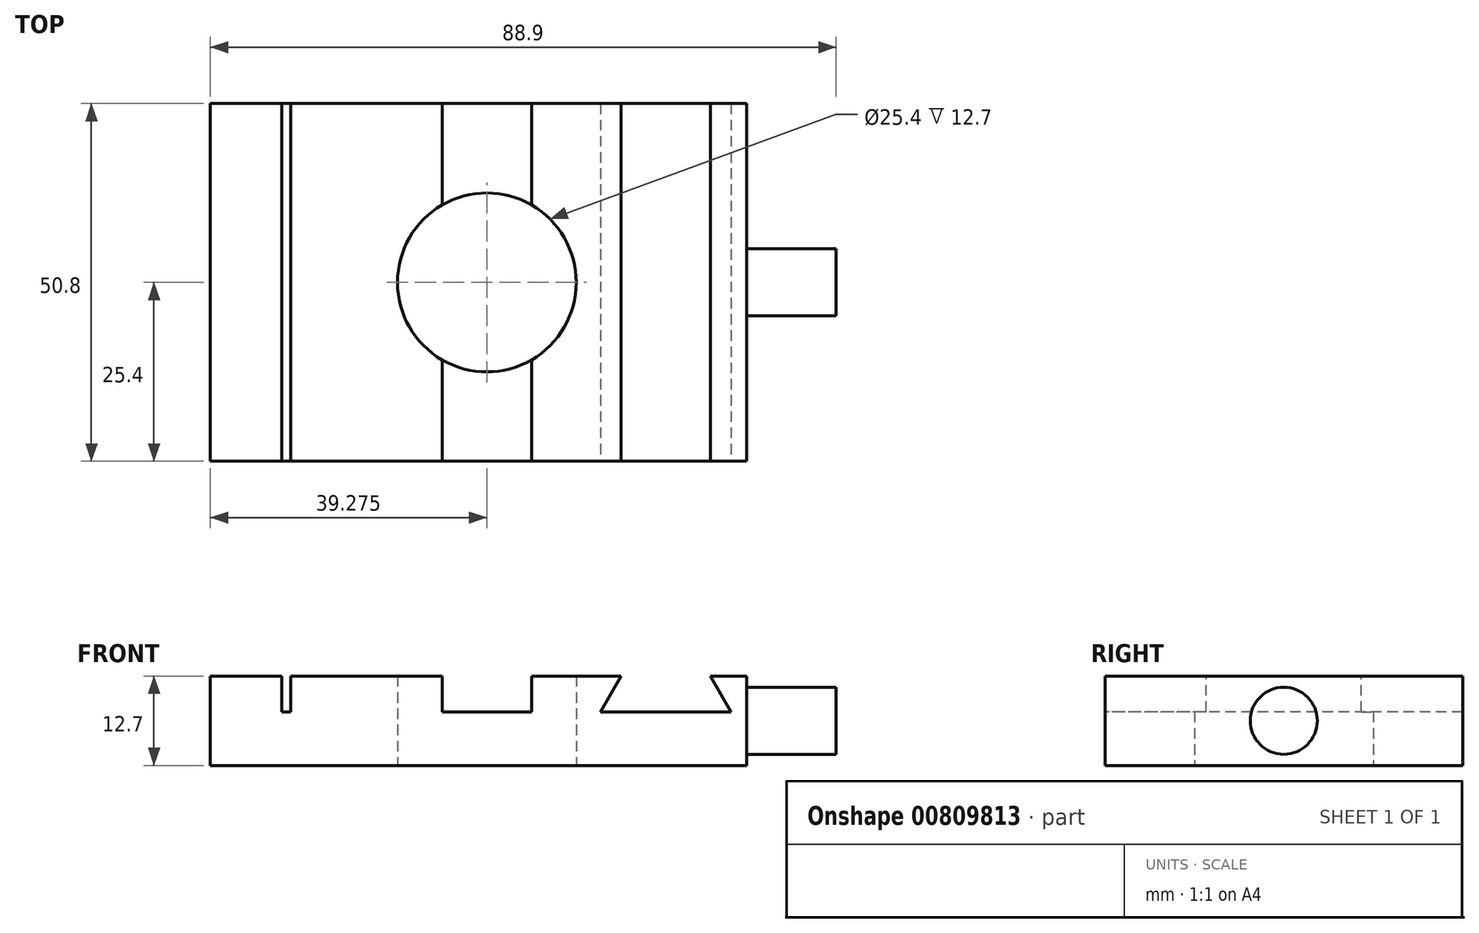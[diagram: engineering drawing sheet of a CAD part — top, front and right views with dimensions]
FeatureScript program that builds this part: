
annotation { "Feature Type Name" : "Feature", "Feature Type Description" : "" }
export const myFeature = defineFeature(function(context is Context, id is Id, definition is map)
    precondition{}
    {
        {
            var Q0;
            Q0=qCreatedBy(makeId("Top.planeOp"),FACE);
            var sketch = newSketch(context, id + "F0", { "sketchPlane" : qUnion([Q0])});
            skLineSegment(sketch, "E0.bottom", {"start": v(-38.1, -25.4) * mm, "end": v(38.1, -25.4) * mm});
            skLineSegment(sketch, "E0.top", {"start": v(-38.1, 25.4) * mm, "end": v(38.1, 25.4) * mm});
            skLineSegment(sketch, "E0.left", {"start": v(-38.1, -25.4) * mm, "end": v(-38.1, 25.4) * mm});
            skLineSegment(sketch, "E0.right", {"start": v(38.1, -25.4) * mm, "end": v(38.1, 25.4) * mm});
            skPoint(sketch, "E0.middle", {"position": v(0, 0) * mm});
            skCircle(sketch, "E1", {"center": v(1.17, 0) * mm, "radius": 12.7 * mm});
            skSolve(sketch);
        }
        {
            var Q0;
            Q0=makeQuery(id+"F0.imprint","IMPRINT",FACE,{"disambiguationData":[TD([[makeQuery(id+"F0.imprint","IMPRINT",EDGE,{"derivedFrom":sQuery(id+"F0.wireOp",EDGE,"E0.bottom")}),1.0]])]});
            extrude(context, id + "F1", {"entities" : qUnion([Q0]), "depth" : 12.7 * mm, "offsetDistance" : 25.4 * mm});
        }
        {
            var Q0;
            Q0=makeQuery(id+"F1.opExtrude","CAP_FACE",FACE,{"disambiguationData":[OSD([sQuery(id+"F0.wireOp",EDGE,"E0.bottom"),sQuery(id+"F0.wireOp",EDGE,"E0.top"),sQuery(id+"F0.wireOp",EDGE,"E0.left"),sQuery(id+"F0.wireOp",EDGE,"E0.right"),sQuery(id+"F0.wireOp",EDGE,"E1")])],"isStart":false});
            var sketch = newSketch(context, id + "F2", { "sketchPlane" : qUnion([Q0])});
            skLineSegment(sketch, "E2.bottom", {"start": v(-27.94, 25.4) * mm, "end": v(-26.67, 25.4) * mm});
            skLineSegment(sketch, "E2.top", {"start": v(-27.94, -25.4) * mm, "end": v(-26.67, -25.4) * mm});
            skLineSegment(sketch, "E2.left", {"start": v(-27.94, 25.4) * mm, "end": v(-27.94, -25.4) * mm});
            skLineSegment(sketch, "E2.right", {"start": v(-26.67, 25.4) * mm, "end": v(-26.67, -25.4) * mm});
            skLineSegment(sketch, "E3", {"start": v(-5.18, 25.4) * mm, "end": v(-5.18, -25.4) * mm});
            skLineSegment(sketch, "E4", {"start": v(-5.18, -25.4) * mm, "end": v(7.52, -25.4) * mm});
            skLineSegment(sketch, "E5", {"start": v(7.52, -25.4) * mm, "end": v(7.52, 25.4) * mm});
            skLineSegment(sketch, "E6", {"start": v(7.52, 25.4) * mm, "end": v(-5.18, 25.4) * mm});
            skLineSegment(sketch, "E7", {"start": v(1.17, 25.4) * mm, "end": v(1.17, -25.4) * mm, "construction": true});
            skPoint(sketch, "E8", {"position": v(1.17, 0) * mm});
            skSolve(sketch);
        }
        {
            var Q0;
            Q0=makeQuery(id+"F2.imprint","IMPRINT",FACE,{"disambiguationData":[TD([[makeQuery(id+"F2.imprint","IMPRINT",EDGE,{"derivedFrom":sQuery(id+"F2.wireOp",EDGE,"E2.bottom")}),-1.0]])]});
            var Q1;
            {var subQ0=sQuery(id+"F2.wireOp",EDGE,"E4");Q1=makeQuery(id+"F2.imprint","IMPRINT",FACE,{"disambiguationData":[TD([[makeQuery(id+"F2.imprint","IMPRINT",EDGE,{"derivedFrom":subQ0}),1.0]])]});}
            var Q2;
            {var subQ0=sQuery(id+"F2.wireOp",EDGE,"E6");Q2=makeQuery(id+"F2.imprint","IMPRINT",FACE,{"disambiguationData":[TD([[makeQuery(id+"F2.imprint","IMPRINT",EDGE,{"derivedFrom":subQ0}),-1.0]])]});}
            extrude(context, id + "F3", {"entities" : qUnion([Q0, Q1, Q2]), "operationType" : NewBodyOperationType.REMOVE, "oppositeDirection" : true, "depth" : 5.08 * mm, "offsetDistance" : 25.4 * mm});
        }
        {
            var Q0;
            Q0=makeQuery(id+"F1.opExtrude","SWEPT_FACE",FACE,{"disambiguationData":[OSD([sQuery(id+"F0.wireOp",EDGE,"E0.bottom")])]});
            var sketch = newSketch(context, id + "F4", { "sketchPlane" : qUnion([Q0])});
            skLineSegment(sketch, "E9", {"start": v(20.22, 12.7) * mm, "end": v(17.3, 7.62) * mm});
            skLineSegment(sketch, "E10", {"start": v(17.3, 7.62) * mm, "end": v(35.86, 7.62) * mm});
            skLineSegment(sketch, "E11", {"start": v(35.86, 7.62) * mm, "end": v(32.92, 12.7) * mm});
            skLineSegment(sketch, "E12", {"start": v(32.92, 12.7) * mm, "end": v(20.22, 12.7) * mm});
            skLineSegment(sketch, "E13", {"start": v(26.57, 7.62) * mm, "end": v(26.57, 12.7) * mm, "construction": true});
            skSolve(sketch);
        }
        {
            var Q0;
            Q0=makeQuery(id+"F4.imprint","IMPRINT",FACE,{"disambiguationData":[TD([[makeQuery(id+"F4.imprint","IMPRINT",EDGE,{"derivedFrom":sQuery(id+"F4.wireOp",EDGE,"E9")}),1.0]])]});
            extrude(context, id + "F5", {"entities" : qUnion([Q0]), "operationType" : NewBodyOperationType.REMOVE, "endBound" : BoundingType.THROUGH_ALL, "oppositeDirection" : true, "depth" : 25.4 * mm, "offsetDistance" : 25.4 * mm});
        }
        {
            var Q0;
            Q0=makeQuery(id+"F1.opExtrude","SWEPT_FACE",FACE,{"disambiguationData":[OSD([sQuery(id+"F0.wireOp",EDGE,"E0.right")])]});
            var sketch = newSketch(context, id + "F6", { "sketchPlane" : qUnion([Q0])});
            skCircle(sketch, "E14", {"center": v(0, 6.35) * mm, "radius": 4.76 * mm});
            skPoint(sketch, "E14.centerSnap0", {"position": v(-25.4, 6.35) * mm});
            skPoint(sketch, "E14.centerSnap1", {"position": v(0, 12.7) * mm});
            skSolve(sketch);
        }
        {
            var Q0;
            Q0 = qSketchRegion(id + "F6", true);
            extrude(context, id + "F7", {"entities" : qUnion([Q0]), "operationType" : NewBodyOperationType.ADD, "depth" : 12.7 * mm, "offsetDistance" : 25.4 * mm});
        }
    });
